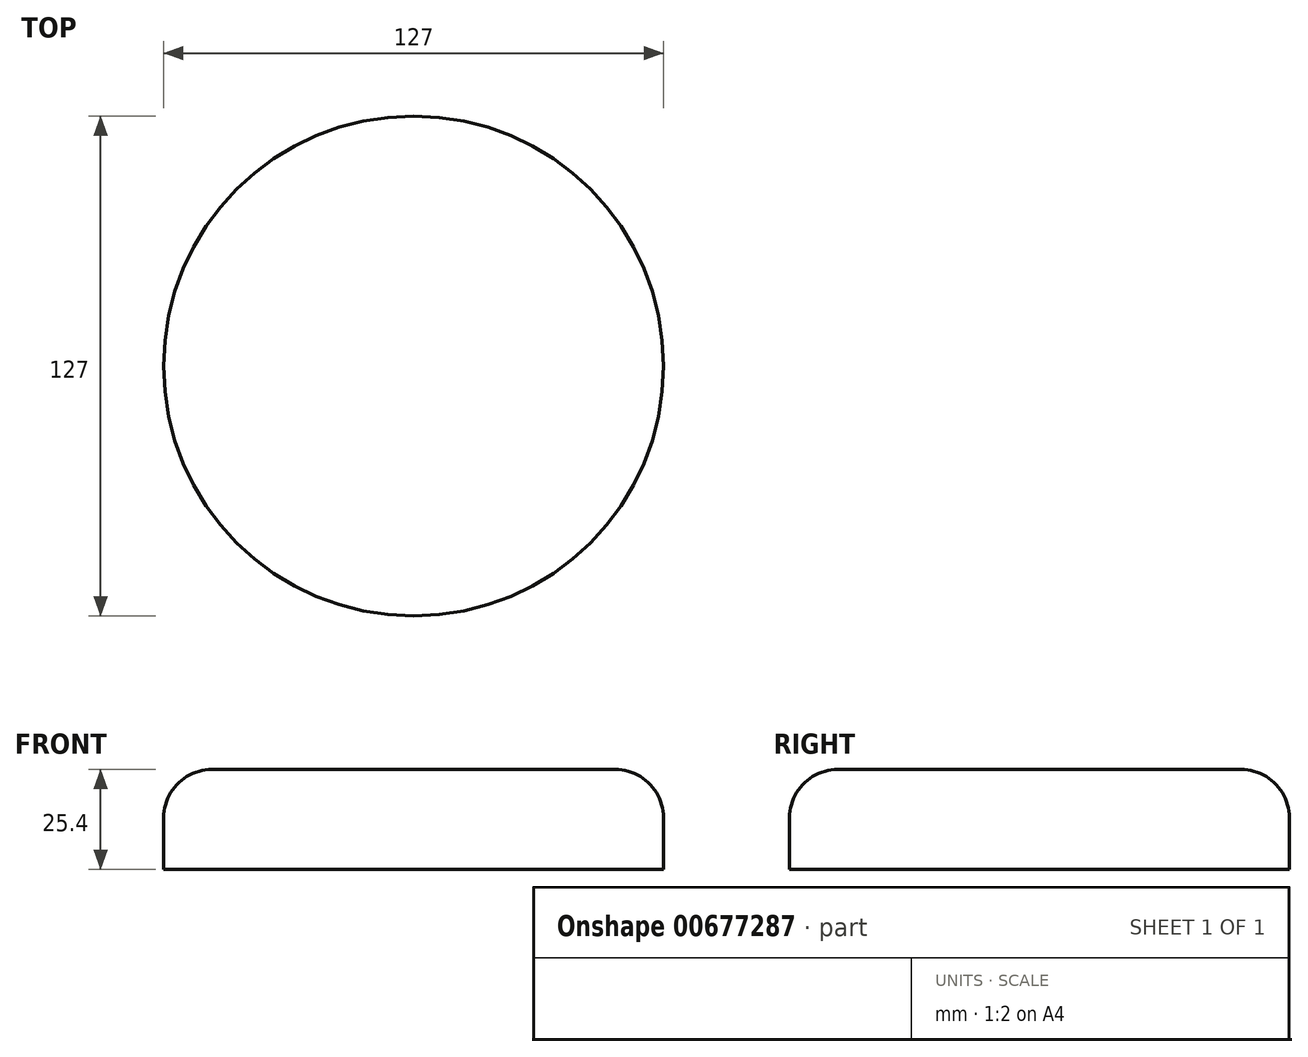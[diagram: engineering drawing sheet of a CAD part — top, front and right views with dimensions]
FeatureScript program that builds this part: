
annotation { "Feature Type Name" : "Feature", "Feature Type Description" : "" }
export const myFeature = defineFeature(function(context is Context, id is Id, definition is map)
    precondition{}
    {
        {
            var Q0;
            Q0=qCreatedBy(makeId("Top.planeOp"),FACE);
            var sketch = newSketch(context, id + "F0", { "sketchPlane" : qUnion([Q0])});
            skCircle(sketch, "E0", {"center": v(0, 0) * mm, "radius": 63.5 * mm});
            skSolve(sketch);
        }
        {
            var Q0;
            Q0=qCreatedBy(makeId("Front.planeOp"),FACE);
            var sketch = newSketch(context, id + "F1", { "sketchPlane" : qUnion([Q0])});
            skSolve(sketch);
        }
        {
            var Q0;
            Q0 = qSketchRegion(id + "F1", true);
            var Q1;
            Q1=makeQuery(id+"F0.imprint","IMPRINT",FACE,{"disambiguationData":[TD([[makeQuery(id+"F0.imprint","IMPRINT",EDGE,{"derivedFrom":sQuery(id+"F0.wireOp",EDGE,"E0")}),1.0]])]});
            extrude(context, id + "F2", {"entities" : qUnion([Q0, Q1]), "depth" : 25.4 * mm, "offsetDistance" : 25.4 * mm});
        }
        {
            var Q0;
            Q0=makeQuery(id+"F2.opExtrude","CAP_EDGE",EDGE,{"disambiguationData":[OSD([sQuery(id+"F0.wireOp",EDGE,"E0")])],"isStart":false});
            fillet(context, id + "F3", {"entities" : qUnion([Q0]), "radius" : 12.26 * mm, "tangentPropagation" : true, "allowEdgeOverflow" : false});
        }
    });
